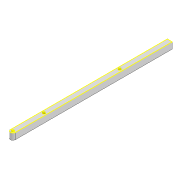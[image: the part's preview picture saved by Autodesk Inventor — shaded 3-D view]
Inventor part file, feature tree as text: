
AUTODESK INVENTOR PART (.ipt)
format: ipt  version: 2022 (Build 260153000, 153)  size: 112,128 bytes
history: native  units: mm
features: sketch x4, extrude x2, projected_geometry x2
ambient origin geometry x8: Origin, YZ Plane, XZ Plane, XY Plane, X Axis, Y Axis, Z Axis, Center Point
bodies: Solid1 (feature_tree)
feature tree (8):
  extrude  "Extrusion1"  Depth=6.0mm
  sketch  "Sketch2"  dims[d2=3.0mm d3=3.0mm]
  extrude  "Extrusion2"  Depth=3.0mm
  sketch  "Sketch4"  dims[d6=3.0mm d7=131.233mm d8=3.0mm d9=37.934mm d10=10.0mm d11=0.0mm]
  sketch  "Sketch1"  dims[d0=347.765mm d1=6.0mm]
  projected_geometry  "Projected Loop1"
  sketch  "Sketch3"  dims[d4=8.0mm d5=0.0mm]
  projected_geometry  "Projected Loop2"
